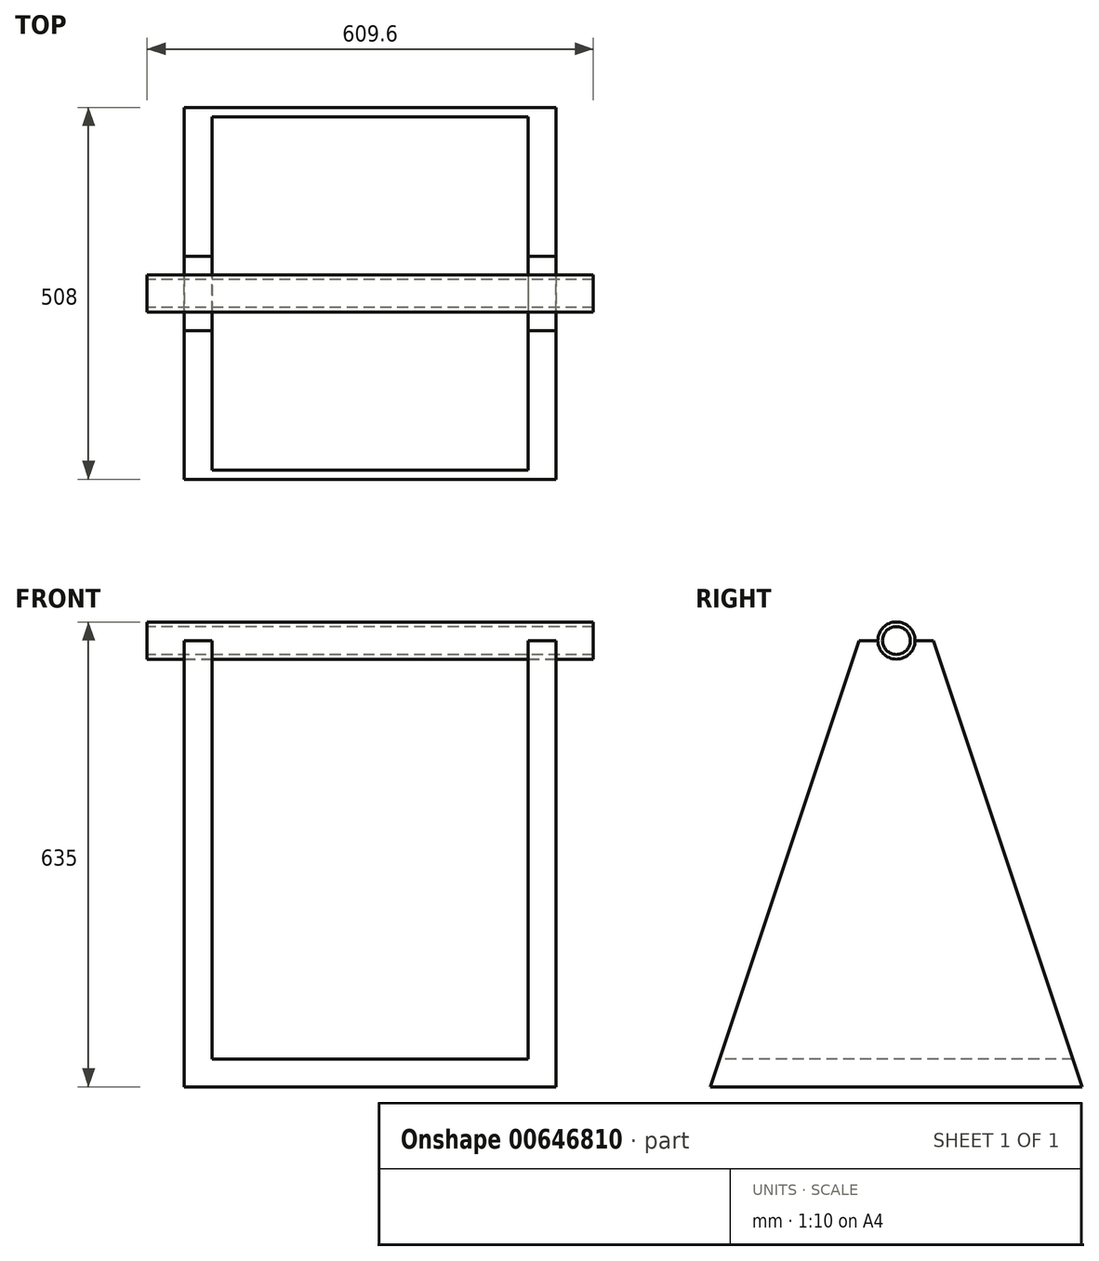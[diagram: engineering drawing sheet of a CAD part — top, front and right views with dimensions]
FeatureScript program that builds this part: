
annotation { "Feature Type Name" : "Feature", "Feature Type Description" : "" }
export const myFeature = defineFeature(function(context is Context, id is Id, definition is map)
    precondition{}
    {
        {
            var Q0;
            Q0=qCreatedBy(makeId("Top.planeOp"),FACE);
            var sketch = newSketch(context, id + "F0", { "sketchPlane" : qUnion([Q0])});
            skLineSegment(sketch, "E0.bottom", {"start": v(254, 254) * mm, "end": v(-254, 254) * mm});
            skLineSegment(sketch, "E0.top", {"start": v(254, -254) * mm, "end": v(-254, -254) * mm});
            skLineSegment(sketch, "E0.left", {"start": v(254, 254) * mm, "end": v(254, -254) * mm});
            skLineSegment(sketch, "E0.right", {"start": v(-254, 254) * mm, "end": v(-254, -254) * mm});
            skPoint(sketch, "E0.middle", {"position": v(0, 0) * mm});
            skSolve(sketch);
        }
        {
            var Q0;
            Q0=makeQuery(id+"F0.imprint","IMPRINT",FACE,{"disambiguationData":[TD([[makeQuery(id+"F0.imprint","IMPRINT",EDGE,{"derivedFrom":sQuery(id+"F0.wireOp",EDGE,"E0.bottom")}),1.0]])]});
            extrude(context, id + "F1", {"entities" : qUnion([Q0]), "depth" : 609.6 * mm, "offsetDistance" : 25.4 * mm});
        }
        {
            var Q0;
            Q0=makeQuery(id+"F1.opExtrude","SWEPT_FACE",FACE,{"disambiguationData":[OSD([sQuery(id+"F0.wireOp",EDGE,"E0.top")])]});
            var sketch = newSketch(context, id + "F2", { "sketchPlane" : qUnion([Q0])});
            skLineSegment(sketch, "E1", {"start": v(215.9, 609.6) * mm, "end": v(215.9, 38.1) * mm});
            skLineSegment(sketch, "E2", {"start": v(215.9, 38.1) * mm, "end": v(-215.9, 38.1) * mm});
            skLineSegment(sketch, "E3", {"start": v(-215.9, 38.1) * mm, "end": v(-215.9, 609.6) * mm});
            skLineSegment(sketch, "E4", {"start": v(-215.9, 609.6) * mm, "end": v(215.9, 609.6) * mm});
            skSolve(sketch);
        }
        {
            var Q0;
            Q0=makeQuery(id+"F2.imprint","IMPRINT",FACE,{"disambiguationData":[TD([[makeQuery(id+"F2.imprint","IMPRINT",EDGE,{"derivedFrom":sQuery(id+"F2.wireOp",EDGE,"E1")}),-1.0]])]});
            extrude(context, id + "F3", {"entities" : qUnion([Q0]), "operationType" : NewBodyOperationType.REMOVE, "endBound" : BoundingType.THROUGH_ALL, "oppositeDirection" : true, "depth" : 25.4 * mm, "offsetDistance" : 25.4 * mm});
        }
        {
            var Q0;
            Q0=makeQuery(id+"F1.opExtrude","SWEPT_FACE",FACE,{"disambiguationData":[OSD([sQuery(id+"F0.wireOp",EDGE,"E0.left")])]});
            var sketch = newSketch(context, id + "F4", { "sketchPlane" : qUnion([Q0])});
            skLineSegment(sketch, "E5", {"start": v(254, 609.6) * mm, "end": v(-254, 609.6) * mm});
            skLineSegment(sketch, "E6", {"start": v(-254, 609.6) * mm, "end": v(-254, 0) * mm});
            skLineSegment(sketch, "E7", {"start": v(-254, 0) * mm, "end": v(-50.8, 609.6) * mm});
            skLineSegment(sketch, "E8", {"start": v(254, 0) * mm, "end": v(50.8, 609.6) * mm});
            skArc(sketch, "E9", {"start": v(-25.4, 609.6) * mm, "mid": v(0, 584.2) * mm, "end": v(25.4, 609.6) * mm});
            skSolve(sketch);
        }
        {
            var Q0;
            {var subQ0=sQuery(id+"F4.wireOp",EDGE,"E6");Q0=makeQuery(id+"F4.imprint","IMPRINT",FACE,{"disambiguationData":[TD([[makeQuery(id+"F4.imprint","IMPRINT",EDGE,{"derivedFrom":subQ0}),1.0]])]});}
            var Q1;
            {var subQ2=sQuery(id+"F4.wireOp",EDGE,"E8");Q1=makeQuery(id+"F4.imprint","IMPRINT",FACE,{"disambiguationData":[TD([[makeQuery(id+"F4.imprint","IMPRINT",EDGE,{"derivedFrom":subQ2}),-1.0]])]});}
            var Q2;
            {var subQ0=sQuery(id+"F4.wireOp",EDGE,"E9");Q2=makeQuery(id+"F4.imprint","IMPRINT",FACE,{"disambiguationData":[TD([[makeQuery(id+"F4.imprint","IMPRINT",EDGE,{"derivedFrom":subQ0}),1.0]])]});}
            extrude(context, id + "F5", {"entities" : qUnion([Q0, Q1, Q2]), "operationType" : NewBodyOperationType.REMOVE, "endBound" : BoundingType.THROUGH_ALL, "oppositeDirection" : true, "depth" : 25.4 * mm, "offsetDistance" : 25.4 * mm});
        }
        {
            var Q0;
            Q0=makeQuery(id+"F1.opExtrude","SWEPT_FACE",FACE,{"disambiguationData":[OSD([sQuery(id+"F0.wireOp",EDGE,"E0.left")])]});
            var sketch = newSketch(context, id + "F6", { "sketchPlane" : qUnion([Q0])});
            skCircle(sketch, "E10", {"center": v(0, 609.6) * mm, "radius": 25.4 * mm});
            skPoint(sketch, "E10.first.point", {"position": v(-25.4, 609.6) * mm});
            skPoint(sketch, "E10.second.point", {"position": v(25.4, 609.6) * mm});
            skPoint(sketch, "E10.third.point", {"position": v(0, 584.2) * mm});
            skSolve(sketch);
        }
        {
            var Q0;
            {var subQ0=sQuery(id+"F6.wireOp",EDGE,"E10");var subQ1=sQuery(id+"F0.wireOp",EDGE,"E0.left");var subQ5=makeQuery(id+"F1.opExtrude","CAP_EDGE",EDGE,{"disambiguationData":[OSD([subQ1])],"isStart":false});var subQ6=makeQuery(id+"F6.imprint","INTERSECT",VERTEX,{"derivedFrom":[makeQuery(id+"F5.boolean.opBoolean","SPLIT",EDGE,{"disambiguationData":[TD([makeQuery(id+"F5.opExtrude","SWEPT_FACE",FACE,{"disambiguationData":[OSD([sQuery(id+"F4.wireOp",EDGE,"E7")])]})])],"derivedFrom":subQ5}),subQ0]});Q0=makeQuery(id+"F6.imprint","IMPRINT",FACE,{"disambiguationData":[TD([[makeQuery(id+"F6.imprint","IMPRINT",EDGE,{"disambiguationData":[TD([[subQ6,1.0]])],"derivedFrom":subQ0}),1.0]])]});}
            extrude(context, id + "F7", {"entities" : qUnion([Q0]), "depth" : 50.8 * mm, "offsetDistance" : 25.4 * mm, "hasSecondDirection" : true, "secondDirectionOppositeDirection" : true, "secondDirectionDepth" : 558.8 * mm});
        }
        {
            var Q0;
            Q0=makeQuery(id+"F7.opExtrude","CAP_FACE",FACE,{"disambiguationData":[OSD([sQuery(id+"F6.wireOp",EDGE,"E10")])],"isStart":false});
            var Q1;
            Q1=makeQuery(id+"F7.opExtrude","CAP_FACE",FACE,{"disambiguationData":[OSD([sQuery(id+"F6.wireOp",EDGE,"E10")])],"isStart":true});
            shell(context, id + "F8", {"entities" : qUnion([Q0, Q1]), "thickness" : 6.35 * mm});
        }
    });
